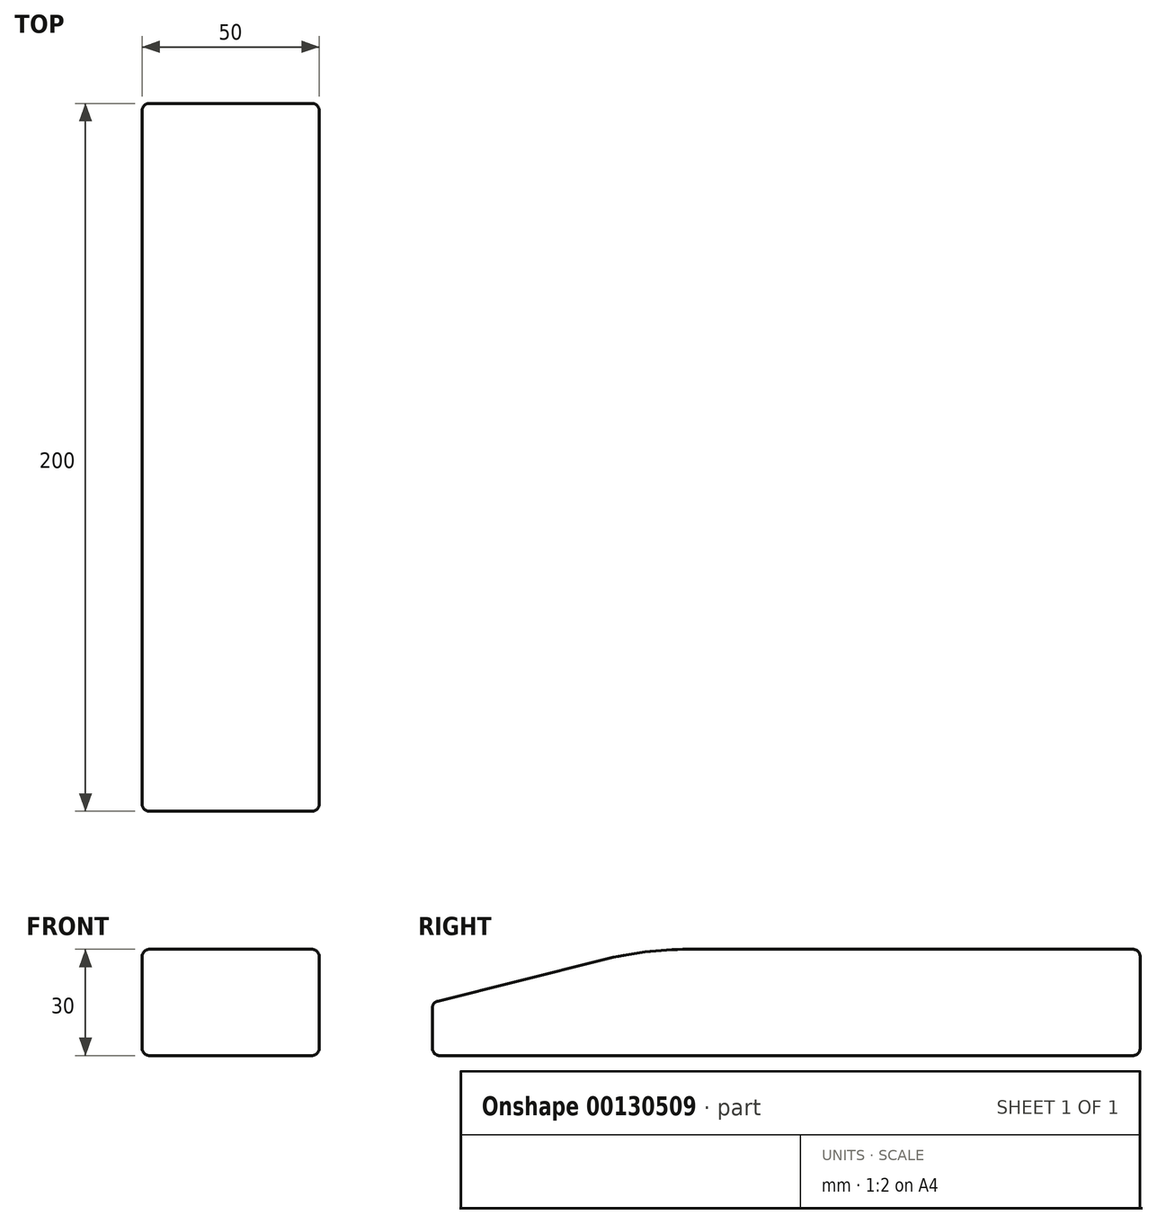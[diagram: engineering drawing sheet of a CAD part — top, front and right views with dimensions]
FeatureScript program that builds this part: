
annotation { "Feature Type Name" : "Feature", "Feature Type Description" : "" }
export const myFeature = defineFeature(function(context is Context, id is Id, definition is map)
    precondition{}
    {
        {
            var Q0;
            Q0=qCreatedBy(makeId("Top.planeOp"),FACE);
            var sketch = newSketch(context, id + "F0", { "sketchPlane" : qUnion([Q0])});
            skLineSegment(sketch, "E0.bottom", {"start": v(0, 0) * mm, "end": v(50, 0) * mm});
            skLineSegment(sketch, "E0.top", {"start": v(0, 200) * mm, "end": v(50, 200) * mm});
            skLineSegment(sketch, "E0.left", {"start": v(0, 0) * mm, "end": v(0, 200) * mm});
            skLineSegment(sketch, "E0.right", {"start": v(50, 0) * mm, "end": v(50, 200) * mm});
            skSolve(sketch);
        }
        {
            var Q0;
            Q0=makeQuery(id+"F0.imprint","IMPRINT",FACE,{"disambiguationData":[TD([[makeQuery(id+"F0.imprint","IMPRINT",EDGE,{"derivedFrom":sQuery(id+"F0.wireOp",EDGE,"E0.bottom")}),1.0]])]});
            extrude(context, id + "F1", {"entities" : qUnion([Q0]), "depth" : 30 * mm});
        }
        {
            var Q0;
            Q0=makeQuery(id+"F1.opExtrude","CAP_EDGE",EDGE,{"disambiguationData":[OSD([sQuery(id+"F0.wireOp",EDGE,"E0.bottom")])],"isStart":false});
            chamfer(context, id + "F2", {"entities" : qUnion([Q0]), "chamferType" : ChamferType.TWO_OFFSETS, "width1" : 60 * mm, "oppositeDirection" : false, "width2" : 15 * mm, "tangentPropagation" : true});
        }
        {
            var Q0;
            {var subQ0=sQuery(id+"F0.wireOp",EDGE,"E0.bottom");Q0=makeQuery(id+"F2.opChamfer","BLEND_EDGE",EDGE,{"blendedFrom":[makeQuery(id+"F1.opExtrude","CAP_EDGE",EDGE,{"disambiguationData":[OSD([subQ0])],"isStart":false}),makeQuery(id+"F1.opExtrude","CAP_FACE",FACE,{"disambiguationData":[OSD([subQ0,sQuery(id+"F0.wireOp",EDGE,"E0.top"),sQuery(id+"F0.wireOp",EDGE,"E0.left"),sQuery(id+"F0.wireOp",EDGE,"E0.right")])],"isStart":false})],"blendedInto":[makeQuery(id+"F1.opExtrude","CAP_FACE",FACE,{"disambiguationData":[OSD([subQ0,sQuery(id+"F0.wireOp",EDGE,"E0.top"),sQuery(id+"F0.wireOp",EDGE,"E0.left"),sQuery(id+"F0.wireOp",EDGE,"E0.right")])],"isStart":false})]});}
            fillet(context, id + "F3", {"entities" : qUnion([Q0]), "radius" : 100 * mm, "tangentPropagation" : true, "allowEdgeOverflow" : false});
        }
        {
            var Q0;
            Q0=makeQuery(id+"F1.opExtrude","SWEPT_FACE",FACE,{"disambiguationData":[OSD([sQuery(id+"F0.wireOp",EDGE,"E0.bottom")])]});
            var Q1;
            Q1=makeQuery(id+"F1.opExtrude","SWEPT_FACE",FACE,{"disambiguationData":[OSD([sQuery(id+"F0.wireOp",EDGE,"E0.right")])]});
            var Q2;
            Q2=makeQuery(id+"F2.opChamfer","BLEND_FACE",FACE,{"disambiguationData":[OSD([sQuery(id+"F0.wireOp",EDGE,"E0.bottom")])]});
            var Q3;
            Q3=makeQuery(id+"F1.opExtrude","SWEPT_EDGE",EDGE,{"disambiguationData":[OSD([sQuery(id+"F0.wireOp",EDGE,"E0.top"),sQuery(id+"F0.wireOp",EDGE,"E0.right")])]});
            var Q4;
            {var subQ0=sQuery(id+"F0.wireOp",EDGE,"E0.bottom");Q4=makeQuery(id+"F2.opChamfer","BLEND_EDGE",EDGE,{"blendedFrom":[makeQuery(id+"F1.opExtrude","CAP_EDGE",EDGE,{"disambiguationData":[OSD([subQ0])],"isStart":false}),makeQuery(id+"F1.opExtrude","SWEPT_FACE",FACE,{"disambiguationData":[OSD([subQ0])]})],"blendedInto":[makeQuery(id+"F1.opExtrude","SWEPT_FACE",FACE,{"disambiguationData":[OSD([subQ0])]})]});}
            var Q5;
            Q5=makeQuery(id+"F1.opExtrude","SWEPT_EDGE",EDGE,{"disambiguationData":[OSD([sQuery(id+"F0.wireOp",EDGE,"E0.bottom"),sQuery(id+"F0.wireOp",EDGE,"E0.right")])]});
            var Q6;
            Q6=makeQuery(id+"F1.opExtrude","CAP_EDGE",EDGE,{"disambiguationData":[OSD([sQuery(id+"F0.wireOp",EDGE,"E0.bottom")])],"isStart":true});
            var Q7;
            Q7=makeQuery(id+"F1.opExtrude","CAP_EDGE",EDGE,{"disambiguationData":[OSD([sQuery(id+"F0.wireOp",EDGE,"E0.right")])],"isStart":true});
            var Q8;
            {var subQ0=sQuery(id+"F0.wireOp",EDGE,"E0.right");var subQ1=sQuery(id+"F0.wireOp",EDGE,"E0.bottom");Q8=makeQuery(id+"F3.opFillet","BLEND_EDGE",EDGE,{"blendedFrom":[makeQuery(id+"F2.opChamfer","BLEND_EDGE",EDGE,{"blendedFrom":[makeQuery(id+"F1.opExtrude","CAP_EDGE",EDGE,{"disambiguationData":[OSD([subQ1])],"isStart":false}),makeQuery(id+"F1.opExtrude","CAP_FACE",FACE,{"disambiguationData":[OSD([subQ1,sQuery(id+"F0.wireOp",EDGE,"E0.top"),sQuery(id+"F0.wireOp",EDGE,"E0.left"),subQ0])],"isStart":false})],"blendedInto":[makeQuery(id+"F1.opExtrude","CAP_FACE",FACE,{"disambiguationData":[OSD([subQ1,sQuery(id+"F0.wireOp",EDGE,"E0.top"),sQuery(id+"F0.wireOp",EDGE,"E0.left"),subQ0])],"isStart":false})]}),makeQuery(id+"F1.opExtrude","SWEPT_FACE",FACE,{"disambiguationData":[OSD([subQ0])]})],"blendedInto":[makeQuery(id+"F1.opExtrude","SWEPT_FACE",FACE,{"disambiguationData":[OSD([subQ0])]})]});}
            var Q9;
            Q9=makeQuery(id+"F2.opChamfer","BLEND_EDGE",EDGE,{"blendedFrom":[makeQuery(id+"F1.opExtrude","CAP_EDGE",EDGE,{"disambiguationData":[OSD([sQuery(id+"F0.wireOp",EDGE,"E0.bottom")])],"isStart":false}),makeQuery(id+"F1.opExtrude","SWEPT_FACE",FACE,{"disambiguationData":[OSD([sQuery(id+"F0.wireOp",EDGE,"E0.right")])]})],"blendedInto":[makeQuery(id+"F1.opExtrude","SWEPT_FACE",FACE,{"disambiguationData":[OSD([sQuery(id+"F0.wireOp",EDGE,"E0.right")])]})]});
            var Q10;
            Q10=makeQuery(id+"F1.opExtrude","CAP_EDGE",EDGE,{"disambiguationData":[OSD([sQuery(id+"F0.wireOp",EDGE,"E0.left")])],"isStart":false});
            var Q11;
            Q11=makeQuery(id+"F1.opExtrude","CAP_EDGE",EDGE,{"disambiguationData":[OSD([sQuery(id+"F0.wireOp",EDGE,"E0.right")])],"isStart":false});
            var Q12;
            {var subQ0=sQuery(id+"F0.wireOp",EDGE,"E0.left");var subQ1=sQuery(id+"F0.wireOp",EDGE,"E0.bottom");Q12=makeQuery(id+"F3.opFillet","BLEND_EDGE",EDGE,{"blendedFrom":[makeQuery(id+"F2.opChamfer","BLEND_EDGE",EDGE,{"blendedFrom":[makeQuery(id+"F1.opExtrude","CAP_EDGE",EDGE,{"disambiguationData":[OSD([subQ1])],"isStart":false}),makeQuery(id+"F1.opExtrude","CAP_FACE",FACE,{"disambiguationData":[OSD([subQ1,sQuery(id+"F0.wireOp",EDGE,"E0.top"),subQ0,sQuery(id+"F0.wireOp",EDGE,"E0.right")])],"isStart":false})],"blendedInto":[makeQuery(id+"F1.opExtrude","CAP_FACE",FACE,{"disambiguationData":[OSD([subQ1,sQuery(id+"F0.wireOp",EDGE,"E0.top"),subQ0,sQuery(id+"F0.wireOp",EDGE,"E0.right")])],"isStart":false})]}),makeQuery(id+"F1.opExtrude","SWEPT_FACE",FACE,{"disambiguationData":[OSD([subQ0])]})],"blendedInto":[makeQuery(id+"F1.opExtrude","SWEPT_FACE",FACE,{"disambiguationData":[OSD([subQ0])]})]});}
            var Q13;
            Q13=makeQuery(id+"F1.opExtrude","SWEPT_EDGE",EDGE,{"disambiguationData":[OSD([sQuery(id+"F0.wireOp",EDGE,"E0.top"),sQuery(id+"F0.wireOp",EDGE,"E0.left")])]});
            var Q14;
            Q14=makeQuery(id+"F1.opExtrude","CAP_EDGE",EDGE,{"disambiguationData":[OSD([sQuery(id+"F0.wireOp",EDGE,"E0.top")])],"isStart":true});
            var Q15;
            Q15=makeQuery(id+"F1.opExtrude","CAP_EDGE",EDGE,{"disambiguationData":[OSD([sQuery(id+"F0.wireOp",EDGE,"E0.top")])],"isStart":false});
            var Q16;
            Q16=makeQuery(id+"F1.opExtrude","CAP_EDGE",EDGE,{"disambiguationData":[OSD([sQuery(id+"F0.wireOp",EDGE,"E0.left")])],"isStart":true});
            var Q17;
            Q17=makeQuery(id+"F1.opExtrude","SWEPT_EDGE",EDGE,{"disambiguationData":[OSD([sQuery(id+"F0.wireOp",EDGE,"E0.bottom"),sQuery(id+"F0.wireOp",EDGE,"E0.left")])]});
            var Q18;
            {var subQ0=sQuery(id+"F0.wireOp",EDGE,"E0.bottom");var subQ1=makeQuery(id+"F1.opExtrude","CAP_FACE",FACE,{"disambiguationData":[OSD([subQ0,sQuery(id+"F0.wireOp",EDGE,"E0.top"),sQuery(id+"F0.wireOp",EDGE,"E0.left"),sQuery(id+"F0.wireOp",EDGE,"E0.right")])],"isStart":false});Q18=makeQuery(id+"F3.opFillet","BLEND_EDGE",EDGE,{"blendedFrom":[makeQuery(id+"F2.opChamfer","BLEND_EDGE",EDGE,{"blendedFrom":[makeQuery(id+"F1.opExtrude","CAP_EDGE",EDGE,{"disambiguationData":[OSD([subQ0])],"isStart":false}),subQ1],"blendedInto":[subQ1]}),subQ1],"blendedInto":[subQ1]});}
            var Q19;
            {var subQ0=sQuery(id+"F0.wireOp",EDGE,"E0.bottom");Q19=makeQuery(id+"F3.opFillet","BLEND_EDGE",EDGE,{"blendedFrom":[makeQuery(id+"F2.opChamfer","BLEND_EDGE",EDGE,{"blendedFrom":[makeQuery(id+"F1.opExtrude","CAP_EDGE",EDGE,{"disambiguationData":[OSD([subQ0])],"isStart":false}),makeQuery(id+"F1.opExtrude","CAP_FACE",FACE,{"disambiguationData":[OSD([subQ0,sQuery(id+"F0.wireOp",EDGE,"E0.top"),sQuery(id+"F0.wireOp",EDGE,"E0.left"),sQuery(id+"F0.wireOp",EDGE,"E0.right")])],"isStart":false})],"blendedInto":[makeQuery(id+"F1.opExtrude","CAP_FACE",FACE,{"disambiguationData":[OSD([subQ0,sQuery(id+"F0.wireOp",EDGE,"E0.top"),sQuery(id+"F0.wireOp",EDGE,"E0.left"),sQuery(id+"F0.wireOp",EDGE,"E0.right")])],"isStart":false})]}),makeQuery(id+"F2.opChamfer","BLEND_FACE",FACE,{"disambiguationData":[OSD([subQ0])]})],"blendedInto":[makeQuery(id+"F2.opChamfer","BLEND_FACE",FACE,{"disambiguationData":[OSD([subQ0])]})]});}
            var Q20;
            Q20=makeQuery(id+"F2.opChamfer","BLEND_EDGE",EDGE,{"blendedFrom":[makeQuery(id+"F1.opExtrude","CAP_EDGE",EDGE,{"disambiguationData":[OSD([sQuery(id+"F0.wireOp",EDGE,"E0.bottom")])],"isStart":false}),makeQuery(id+"F1.opExtrude","SWEPT_FACE",FACE,{"disambiguationData":[OSD([sQuery(id+"F0.wireOp",EDGE,"E0.left")])]})],"blendedInto":[makeQuery(id+"F1.opExtrude","SWEPT_FACE",FACE,{"disambiguationData":[OSD([sQuery(id+"F0.wireOp",EDGE,"E0.left")])]})]});
            fillet(context, id + "F4", {"entities" : qUnion([Q0, Q1, Q2, Q3, Q4, Q5, Q6, Q7, Q8, Q9, Q10, Q11, Q12, Q13, Q14, Q15, Q16, Q17, Q18, Q19, Q20]), "radius" : 2 * mm, "tangentPropagation" : true, "allowEdgeOverflow" : false});
        }
    });
